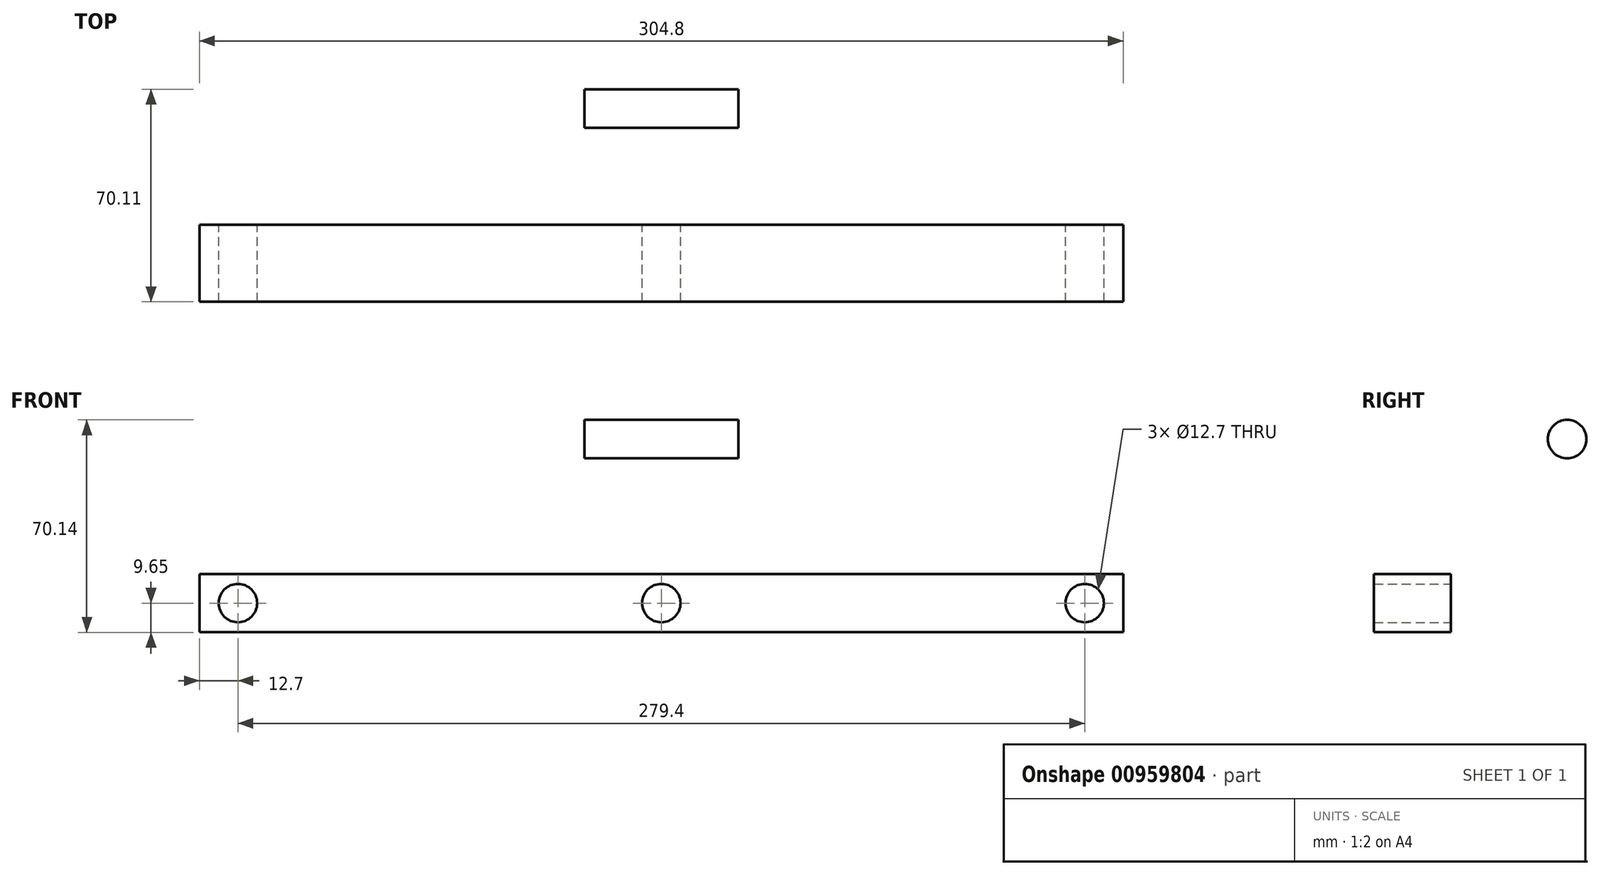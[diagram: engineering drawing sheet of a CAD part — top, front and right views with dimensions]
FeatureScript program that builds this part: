
annotation { "Feature Type Name" : "Feature", "Feature Type Description" : "" }
export const myFeature = defineFeature(function(context is Context, id is Id, definition is map)
    precondition{}
    {
        {
            var Q0;
            Q0=qCreatedBy(makeId("Front.planeOp"),FACE);
            var sketch = newSketch(context, id + "F0", { "sketchPlane" : qUnion([Q0])});
            skLineSegment(sketch, "E0.bottom", {"start": v(152.4, 9.65) * mm, "end": v(-152.4, 9.65) * mm});
            skLineSegment(sketch, "E0.top", {"start": v(152.4, -9.65) * mm, "end": v(-152.4, -9.65) * mm});
            skLineSegment(sketch, "E0.left", {"start": v(152.4, 9.65) * mm, "end": v(152.4, -9.65) * mm});
            skLineSegment(sketch, "E0.right", {"start": v(-152.4, 9.65) * mm, "end": v(-152.4, -9.65) * mm});
            skPoint(sketch, "E0.middle", {"position": v(0, 0) * mm});
            skCircle(sketch, "E1", {"center": v(-139.7, 0) * mm, "radius": 6.35 * mm});
            skCircle(sketch, "E2", {"center": v(139.7, 0) * mm, "radius": 6.35 * mm});
            skLineSegment(sketch, "E3", {"start": v(0, 9.65) * mm, "end": v(0, 53.16) * mm});
            skCircle(sketch, "E4", {"center": v(0, 0) * mm, "radius": 6.35 * mm});
            skSolve(sketch);
        }
        {
            var Q0;
            Q0=makeQuery(id+"F0.imprint","IMPRINT",FACE,{"disambiguationData":[TD([[makeQuery(id+"F0.imprint","IMPRINT",EDGE,{"derivedFrom":sQuery(id+"F0.wireOp",EDGE,"E0.top")}),-1.0]])]});
            extrude(context, id + "F1", {"entities" : qUnion([Q0]), "endBound" : BoundingType.SYMMETRIC, "depth" : 25.4 * mm, "offsetDistance" : 25.4 * mm});
        }
        {
            var Q0;
            Q0=qCreatedBy(makeId("Right.planeOp"),FACE);
            var sketch = newSketch(context, id + "F2", { "sketchPlane" : qUnion([Q0])});
            skCircle(sketch, "E5", {"center": v(51.06, 54.14) * mm, "radius": 6.35 * mm});
            skSolve(sketch);
        }
        {
            var Q0;
            Q0=makeQuery(id+"F2.imprint","IMPRINT",FACE,{"disambiguationData":[TD([[makeQuery(id+"F2.imprint","IMPRINT",EDGE,{"derivedFrom":sQuery(id+"F2.wireOp",EDGE,"E5")}),1.0]])]});
            extrude(context, id + "F3", {"entities" : qUnion([Q0]), "endBound" : BoundingType.SYMMETRIC, "depth" : 50.8 * mm, "offsetDistance" : 25.4 * mm});
        }
    });
